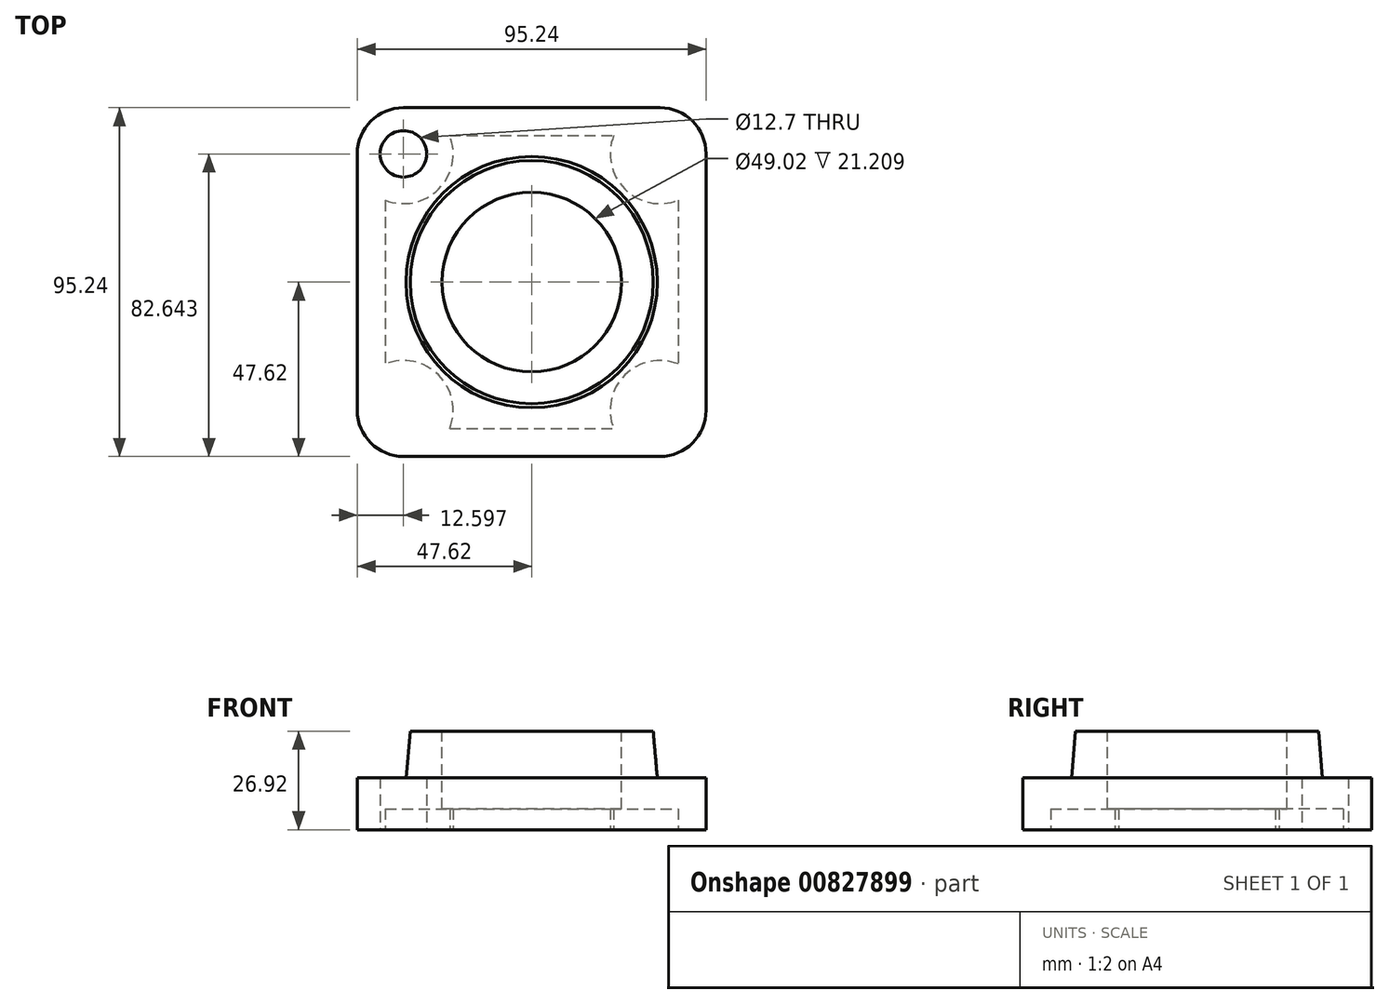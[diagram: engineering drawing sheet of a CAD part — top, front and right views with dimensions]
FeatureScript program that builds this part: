
annotation { "Feature Type Name" : "Feature", "Feature Type Description" : "" }
export const myFeature = defineFeature(function(context is Context, id is Id, definition is map)
    precondition{}
    {
        {
            var Q0;
            Q0=qCreatedBy(makeId("Top.planeOp"),FACE);
            var sketch = newSketch(context, id + "F0", { "sketchPlane" : qUnion([Q0])});
            skLineSegment(sketch, "E0.bottom", {"start": v(-35.02, 47.63) * mm, "end": v(35.02, 47.63) * mm});
            skLineSegment(sketch, "E0.top", {"start": v(-35.02, -47.63) * mm, "end": v(35.02, -47.63) * mm});
            skLineSegment(sketch, "E0.left", {"start": v(-47.63, 35.02) * mm, "end": v(-47.63, -35.02) * mm});
            skLineSegment(sketch, "E0.right", {"start": v(47.63, 35.02) * mm, "end": v(47.63, -35.02) * mm});
            skPoint(sketch, "E0.middle", {"position": v(0, 0) * mm});
            skLineSegment(sketch, "E1", {"start": v(-47.63, 47.63) * mm, "end": v(47.63, -47.63) * mm, "construction": true});
            skLineSegment(sketch, "E2", {"start": v(47.63, 47.63) * mm, "end": v(-47.63, -47.63) * mm, "construction": true});
            skPoint(sketch, "E3", {"position": v(-35.02, 35.02) * mm});
            skCircle(sketch, "E4", {"center": v(-35.02, 35.02) * mm, "radius": 6.35 * mm, "construction": true});
            skLineSegment(sketch, "E5.top", {"start": v(-22.38, -40) * mm, "end": v(22.38, -40) * mm});
            skLineSegment(sketch, "E5.right", {"start": v(40, 22.38) * mm, "end": v(40, -22.38) * mm});
            skArc(sketch, "E6", {"start": v(-22.38, 40) * mm, "mid": v(-25.41, 25.41) * mm, "end": v(-40, 22.38) * mm});
            skArc(sketch, "E7", {"start": v(-47.63, 35.02) * mm, "mid": v(-43.93, 43.93) * mm, "end": v(-35.02, 47.62) * mm});
            skArc(sketch, "E8.1.0", {"start": v(35.02, 47.63) * mm, "mid": v(43.93, 43.93) * mm, "end": v(47.62, 35.02) * mm});
            skArc(sketch, "E8.1.1", {"start": v(40, 22.38) * mm, "mid": v(25.41, 25.41) * mm, "end": v(22.38, 40) * mm});
            skArc(sketch, "E8.2.0", {"start": v(47.63, -35.02) * mm, "mid": v(43.93, -43.93) * mm, "end": v(35.02, -47.62) * mm});
            skArc(sketch, "E8.2.1", {"start": v(22.38, -40) * mm, "mid": v(25.41, -25.41) * mm, "end": v(40, -22.38) * mm});
            skArc(sketch, "E8.3.0", {"start": v(-35.02, -47.63) * mm, "mid": v(-43.93, -43.93) * mm, "end": v(-47.62, -35.02) * mm});
            skArc(sketch, "E8.3.1", {"start": v(-40, -22.38) * mm, "mid": v(-25.41, -25.41) * mm, "end": v(-22.38, -40) * mm});
            skLineSegment(sketch, "E8.anchor1", {"start": v(0, 0) * mm, "end": v(-47.63, 35.02) * mm, "construction": true});
            skLineSegment(sketch, "E8.anchor2", {"start": v(0, 0) * mm, "end": v(-35.02, -47.63) * mm, "construction": true});
            skPoint(sketch, "E9.orphan", {"position": v(40, 40) * mm});
            skPoint(sketch, "E10.orphan", {"position": v(40, -40) * mm});
            skPoint(sketch, "E11.orphan", {"position": v(-40, -40) * mm});
            skLineSegment(sketch, "E12.trimOffspring", {"start": v(-22.38, 40) * mm, "end": v(22.38, 40) * mm});
            skPoint(sketch, "E5.left.start.orphan", {"position": v(-40, 40) * mm});
            skLineSegment(sketch, "E13.trimOffspring", {"start": v(-40, 22.38) * mm, "end": v(-40, -22.38) * mm});
            skSolve(sketch);
        }
        {
            var Q0;
            Q0=makeQuery(id+"F0.imprint","IMPRINT",FACE,{"disambiguationData":[TD([[makeQuery(id+"F0.imprint","IMPRINT",EDGE,{"derivedFrom":sQuery(id+"F0.wireOp",EDGE,"E0.bottom")}),-1.0]])]});
            var Q1;
            Q1=makeQuery(id+"F0.imprint","IMPRINT",FACE,{"disambiguationData":[TD([[makeQuery(id+"F0.imprint","IMPRINT",EDGE,{"derivedFrom":sQuery(id+"F0.wireOp",EDGE,"E5.top")}),1.0]])]});
            extrude(context, id + "F1", {"entities" : qUnion([Q0, Q1]), "depth" : 14.22 * mm, "offsetDistance" : 25.4 * mm});
        }
        {
            var Q0;
            Q0=makeQuery(id+"F0.imprint","IMPRINT",FACE,{"disambiguationData":[TD([[makeQuery(id+"F0.imprint","IMPRINT",EDGE,{"derivedFrom":sQuery(id+"F0.wireOp",EDGE,"E5.top")}),1.0]])]});
            extrude(context, id + "F2", {"entities" : qUnion([Q0]), "operationType" : NewBodyOperationType.REMOVE, "depth" : 5.7 * mm, "offsetDistance" : 25.4 * mm});
        }
        {
            var Q0;
            Q0=sQuery(id+"F0.wireOp",VERTEX,"E3");
            var Q1;
            Q1=makeQuery(id+"F1.opExtrude","SWEPT_BODY",BODY,{"disambiguationData":[OSD([sQuery(id+"F0.wireOp",EDGE,"E0.bottom"),sQuery(id+"F0.wireOp",EDGE,"E0.top"),sQuery(id+"F0.wireOp",EDGE,"E0.left"),sQuery(id+"F0.wireOp",EDGE,"E0.right"),sQuery(id+"F0.wireOp",EDGE,"E7"),sQuery(id+"F0.wireOp",EDGE,"E8.1.0"),sQuery(id+"F0.wireOp",EDGE,"E8.2.0"),sQuery(id+"F0.wireOp",EDGE,"E8.3.0")])]});
            hole(context, id + "F3", {"style" : HoleStyle.SIMPLE, "endStyle" : HoleEndStyle.THROUGH, "oppositeDirection" : true, "holeDiameter" : 12.7 * mm, "majorDiameter" : 6.35 * mm, "isTappedThrough" : true, "tappedDepth" : 12.7 * mm, "tapClearance" : 3, "locations" : qUnion([Q0]), "scope" : qUnion([Q1])});
        }
        {
            var Q0;
            Q0=qCreatedBy(makeId("Right.planeOp"),FACE);
            var sketch = newSketch(context, id + "F4", { "sketchPlane" : qUnion([Q0])});
            skLineSegment(sketch, "E14", {"start": v(0, 0) * mm, "end": v(0, 65.38) * mm, "construction": true});
            skSolve(sketch);
        }
        {
            var Q0;
            Q0=makeQuery(id+"F1.opExtrude","CAP_FACE",FACE,{"disambiguationData":[OSD([sQuery(id+"F0.wireOp",EDGE,"E0.bottom"),sQuery(id+"F0.wireOp",EDGE,"E0.top"),sQuery(id+"F0.wireOp",EDGE,"E0.left"),sQuery(id+"F0.wireOp",EDGE,"E0.right"),sQuery(id+"F0.wireOp",EDGE,"E7"),sQuery(id+"F0.wireOp",EDGE,"E8.1.0"),sQuery(id+"F0.wireOp",EDGE,"E8.2.0"),sQuery(id+"F0.wireOp",EDGE,"E8.3.0")])],"isStart":false});
            var sketch = newSketch(context, id + "F5", { "sketchPlane" : qUnion([Q0])});
            skCircle(sketch, "E15", {"center": v(0, 0) * mm, "radius": 34.3 * mm});
            skSolve(sketch);
        }
        {
            var Q0;
            Q0 = qSketchRegion(id + "F5", true);
            extrude(context, id + "F6", {"entities" : qUnion([Q0]), "operationType" : NewBodyOperationType.ADD, "depth" : 12.7 * mm, "offsetDistance" : 25.4 * mm, "hasDraft" : true, "draftAngle" : 5 * degree, "draftPullDirection" : true});
        }
        {
            var Q0;
            Q0=sQuery(id+"F5.wireOp",VERTEX,"E15.center");
            var Q1;
            Q1=makeQuery(id+"F1.opExtrude","SWEPT_BODY",BODY,{"disambiguationData":[OSD([sQuery(id+"F0.wireOp",EDGE,"E0.bottom"),sQuery(id+"F0.wireOp",EDGE,"E0.top"),sQuery(id+"F0.wireOp",EDGE,"E0.left"),sQuery(id+"F0.wireOp",EDGE,"E0.right"),sQuery(id+"F0.wireOp",EDGE,"E7"),sQuery(id+"F0.wireOp",EDGE,"E8.1.0"),sQuery(id+"F0.wireOp",EDGE,"E8.2.0"),sQuery(id+"F0.wireOp",EDGE,"E8.3.0")])]});
            hole(context, id + "F7", {"style" : HoleStyle.SIMPLE, "endStyle" : HoleEndStyle.THROUGH, "holeDiameter" : 49.02 * mm, "majorDiameter" : 6.35 * mm, "isTappedThrough" : true, "tappedDepth" : 12.7 * mm, "tapClearance" : 3, "locations" : qUnion([Q0]), "scope" : qUnion([Q1])});
        }
        {
            var Q0;
            Q0=sQuery(id+"F5.wireOp",VERTEX,"E15.center");
            var Q1;
            Q1=makeQuery(id+"F1.opExtrude","SWEPT_BODY",BODY,{"disambiguationData":[OSD([sQuery(id+"F0.wireOp",EDGE,"E0.bottom"),sQuery(id+"F0.wireOp",EDGE,"E0.top"),sQuery(id+"F0.wireOp",EDGE,"E0.left"),sQuery(id+"F0.wireOp",EDGE,"E0.right"),sQuery(id+"F0.wireOp",EDGE,"E7"),sQuery(id+"F0.wireOp",EDGE,"E8.1.0"),sQuery(id+"F0.wireOp",EDGE,"E8.2.0"),sQuery(id+"F0.wireOp",EDGE,"E8.3.0")])]});
            hole(context, id + "F8", {"style" : HoleStyle.SIMPLE, "endStyle" : HoleEndStyle.THROUGH, "oppositeDirection" : true, "holeDiameter" : 49.02 * mm, "majorDiameter" : 6.35 * mm, "isTappedThrough" : true, "tappedDepth" : 12.7 * mm, "tapClearance" : 3, "locations" : qUnion([Q0]), "scope" : qUnion([Q1])});
        }
    });
